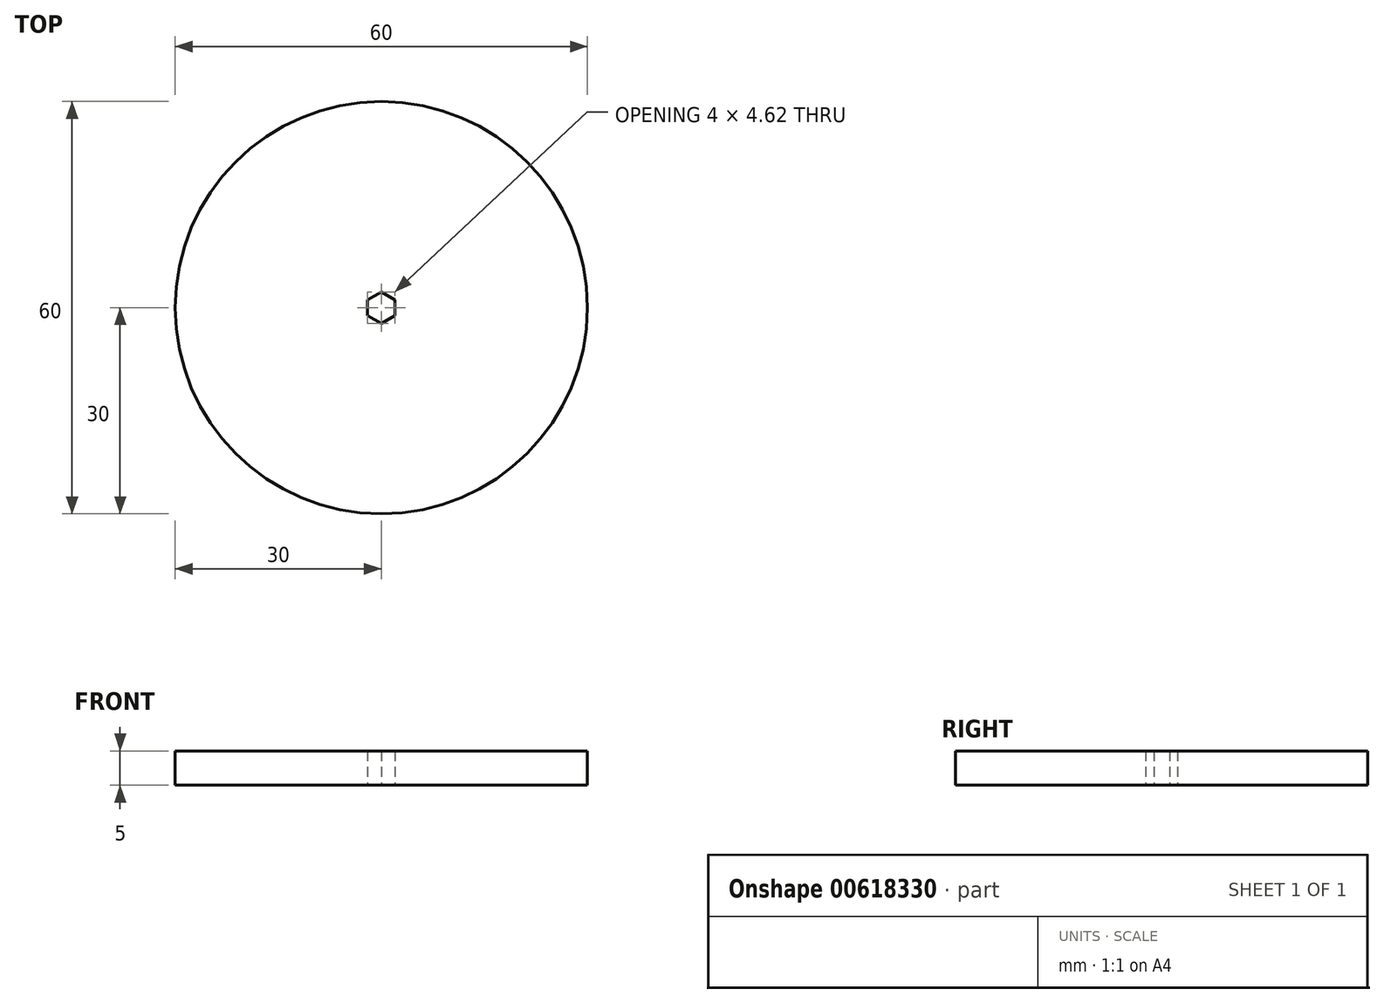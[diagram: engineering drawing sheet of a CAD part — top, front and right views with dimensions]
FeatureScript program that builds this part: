
annotation { "Feature Type Name" : "Feature", "Feature Type Description" : "" }
export const myFeature = defineFeature(function(context is Context, id is Id, definition is map)
    precondition{}
    {
        {
            var Q0;
            Q0=qCreatedBy(makeId("Top.planeOp"),FACE);
            var sketch = newSketch(context, id + "F0", { "sketchPlane" : qUnion([Q0])});
            skCircle(sketch, "E0", {"center": v(0, 0) * mm, "radius": 30 * mm});
            skCircle(sketch, "E1", {"center": v(0, 0) * mm, "radius": 2 * mm});
            skCircle(sketch, "E2.cCircle", {"center": v(0, 0) * mm, "radius": 2 * mm, "construction": true});
            skLineSegment(sketch, "E2.0", {"start": v(2, 1.15) * mm, "end": v(2, -1.15) * mm});
            skLineSegment(sketch, "E2.1", {"start": v(2, -1.15) * mm, "end": v(0, -2.3) * mm});
            skLineSegment(sketch, "E2.2", {"start": v(0, -2.3) * mm, "end": v(-2, -1.15) * mm});
            skLineSegment(sketch, "E2.3", {"start": v(-2, -1.15) * mm, "end": v(-2, 1.15) * mm});
            skLineSegment(sketch, "E2.4", {"start": v(-2, 1.15) * mm, "end": v(0, 2.3) * mm});
            skLineSegment(sketch, "E2.5", {"start": v(0, 2.3) * mm, "end": v(2, 1.15) * mm});
            skPoint(sketch, "E2.0.midPoint", {"position": v(2, 0) * mm});
            skSolve(sketch);
        }
        {
            var Q0;
            Q0=makeQuery(id+"F0.imprint","IMPRINT",FACE,{"disambiguationData":[TD([[makeQuery(id+"F0.imprint","IMPRINT",EDGE,{"derivedFrom":sQuery(id+"F0.wireOp",EDGE,"E0")}),1.0]])]});
            extrude(context, id + "F1", {"entities" : qUnion([Q0]), "depth" : 5 * mm, "offsetDistance" : 25 * mm});
        }
    });
